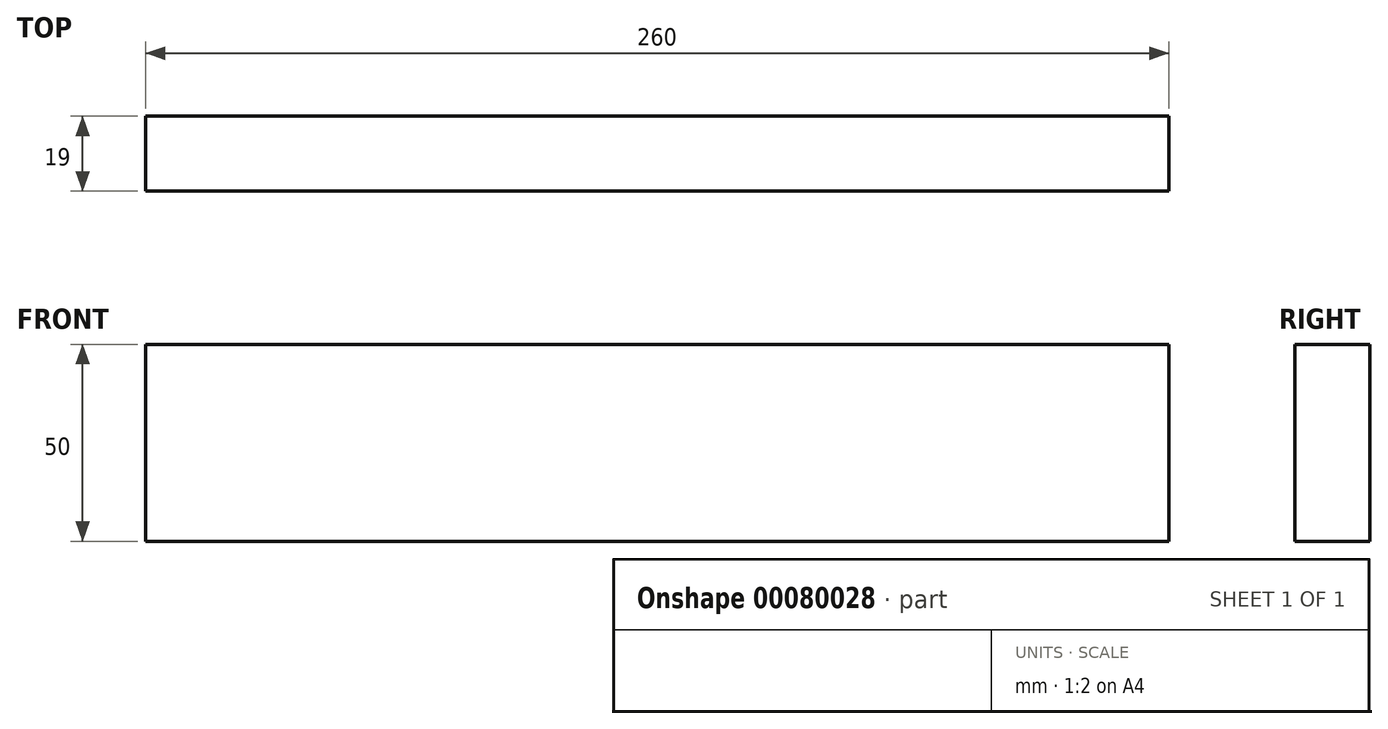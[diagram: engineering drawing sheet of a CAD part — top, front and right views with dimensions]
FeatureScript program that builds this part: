
annotation { "Feature Type Name" : "Feature", "Feature Type Description" : "" }
export const myFeature = defineFeature(function(context is Context, id is Id, definition is map)
    precondition{}
    {
        {
            var Q0;
            Q0=qCreatedBy(makeId("Front.planeOp"),FACE);
            var sketch = newSketch(context, id + "F0", { "sketchPlane" : qUnion([Q0])});
            skLineSegment(sketch, "E0.bottom", {"start": v(0, 0) * mm, "end": v(260, 0) * mm});
            skLineSegment(sketch, "E0.top", {"start": v(0, -50) * mm, "end": v(260, -50) * mm});
            skLineSegment(sketch, "E0.left", {"start": v(0, 0) * mm, "end": v(0, -50) * mm});
            skLineSegment(sketch, "E0.right", {"start": v(260, 0) * mm, "end": v(260, -50) * mm});
            skSolve(sketch);
        }
        {
            var Q0;
            Q0=makeQuery(id+"F0.imprint","IMPRINT",FACE,{"disambiguationData":[TD([[makeQuery(id+"F0.imprint","IMPRINT",EDGE,{"derivedFrom":sQuery(id+"F0.wireOp",EDGE,"E0.bottom")}),-1.0]])]});
            extrude(context, id + "F1", {"entities" : qUnion([Q0]), "depth" : 19 * mm});
        }
    });
